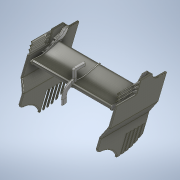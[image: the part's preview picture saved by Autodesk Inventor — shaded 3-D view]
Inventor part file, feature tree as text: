
AUTODESK INVENTOR PART (.ipt)
format: ipt  version: 2022 (Build 260153000, 153)  size: 5,445,632 bytes
history: native  units: in
note: dims shown in document units (in); Inventor stores cm internally (conversion verified against a paired STEP export)
features: extrude x8, sketch x6, other x5, fillet x4, mirror x3
ambient origin geometry x8: Origin, YZ Plane, XZ Plane, XY Plane, X Axis, Y Axis, Z Axis, Center Point
bodies: Solido2 (feature_tree), Solido8 (feature_tree)
feature tree (26):
  sketch  "Schizzo27"
  extrude  "Estrusione16"  Depth=0.7874in TaperAngle=0.0deg
  mirror  "Specchio3"
  extrude  "Estrusione17"  Depth=0.7874in TaperAngle=0.0deg
  extrude  "Estrusione18"  Depth=1.1811in TaperAngle=0.0deg
  other  "Elimina faccia16"
  other  "Elimina faccia17"
  extrude  "Estrusione19"  Depth=0.0039in TaperAngle=0.0deg
  extrude  "Estrusione20"  Depth=0.1969in
  other  "Piano di lavoro17"
  mirror  "Specchio4"
  extrude  "Estrusione21"  Depth=0.4724in
  mirror  "Specchio5"
  fillet  "Raccordo4"  Radius=0.4724in
  fillet  "Raccordo5"  Radius=0.0984in
  fillet  "Raccordo6"  [1 undecoded]
  other  "Piano di lavoro18"
  other  "Elimina faccia18"
  extrude  "Estrusione22"  TaperAngle=0.0deg  [1 undecoded]
  extrude  "Estrusione23"  Depth=8.2283in
  sketch  "Schizzo28"
  sketch  "Schizzo29"
  sketch  "Schizzo30"
  sketch  "Schizzo32"
  sketch  "Schizzo33"
  fillet  "Fillet30"  Radius=8.248in
note: 2 required parameter values undecoded (feature->parameter linkage not recoverable at this tier; creation-order binding heuristic only, values carry confidence <= 0.55)
